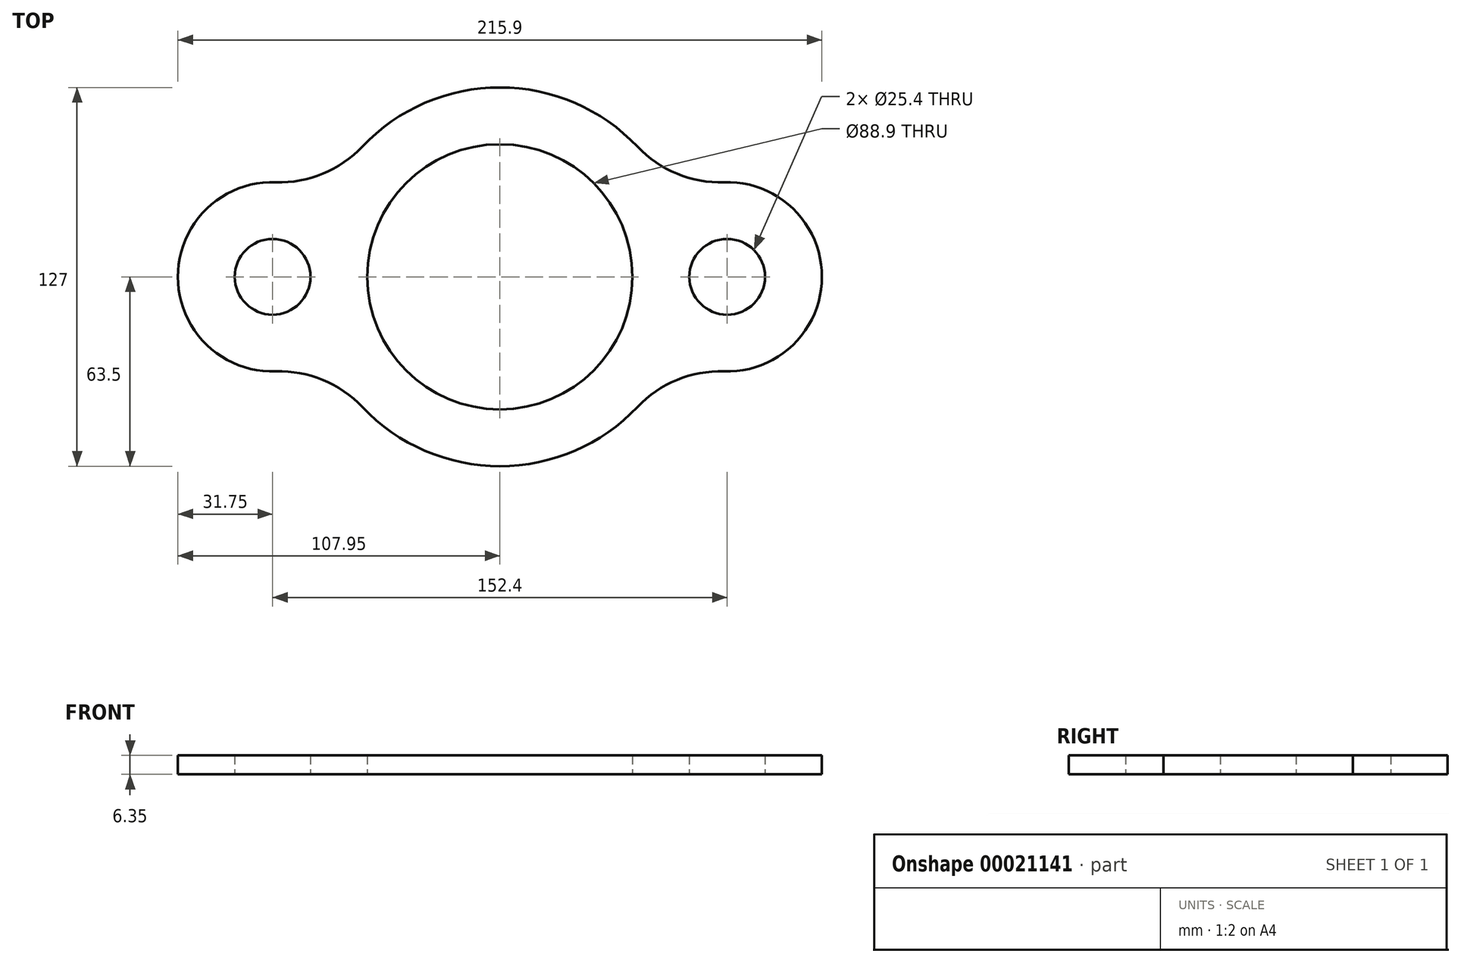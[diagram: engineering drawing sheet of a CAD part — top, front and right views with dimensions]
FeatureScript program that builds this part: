
annotation { "Feature Type Name" : "Feature", "Feature Type Description" : "" }
export const myFeature = defineFeature(function(context is Context, id is Id, definition is map)
    precondition{}
    {
        {
            var Q0;
            Q0=qCreatedBy(makeId("Top.planeOp"),FACE);
            var sketch = newSketch(context, id + "F0", { "sketchPlane" : qUnion([Q0])});
            skArc(sketch, "E0", {"start": v(-46.14, -43.63) * mm, "mid": v(0, -63.5) * mm, "end": v(46.14, -43.63) * mm});
            skCircle(sketch, "E1", {"center": v(0, 0) * mm, "radius": 44.45 * mm});
            skLineSegment(sketch, "E2", {"start": v(0, 0) * mm, "end": v(-113.89, 0) * mm});
            skLineSegment(sketch, "E3", {"start": v(-113.89, 0) * mm, "end": v(113.62, 0) * mm});
            skCircle(sketch, "E4", {"center": v(-76.2, 0) * mm, "radius": 12.7 * mm});
            skCircle(sketch, "E5", {"center": v(76.2, 0) * mm, "radius": 12.7 * mm});
            skArc(sketch, "E6", {"start": v(-75.12, 31.73) * mm, "mid": v(-107.95, 0) * mm, "end": v(-75.12, -31.73) * mm});
            skArc(sketch, "E7", {"start": v(75.12, -31.73) * mm, "mid": v(107.95, 0) * mm, "end": v(75.12, 31.73) * mm});
            skArc(sketch, "E8.trimOffspring", {"start": v(46.14, 43.63) * mm, "mid": v(0, 63.5) * mm, "end": v(-46.14, 43.63) * mm});
            skPoint(sketch, "E9.visualSharp", {"position": v(-57.94, -25.98) * mm});
            skArc(sketch, "E9.filletArc", {"start": v(-46.14, -43.63) * mm, "mid": v(-59.35, -34.56) * mm, "end": v(-75.12, -31.73) * mm});
            skPoint(sketch, "E10.visualSharp", {"position": v(-57.94, 25.98) * mm});
            skArc(sketch, "E10.filletArc", {"start": v(-75.12, 31.73) * mm, "mid": v(-59.35, 34.56) * mm, "end": v(-46.14, 43.63) * mm});
            skPoint(sketch, "E11.visualSharp", {"position": v(57.94, 25.98) * mm});
            skArc(sketch, "E11.filletArc", {"start": v(46.14, 43.63) * mm, "mid": v(59.35, 34.56) * mm, "end": v(75.12, 31.73) * mm});
            skPoint(sketch, "E12.visualSharp", {"position": v(57.94, -25.98) * mm});
            skArc(sketch, "E12.filletArc", {"start": v(75.12, -31.73) * mm, "mid": v(59.35, -34.56) * mm, "end": v(46.14, -43.63) * mm});
            skSolve(sketch);
        }
        {
            var Q0;
            Q0=makeQuery(id+"F0.imprint","IMPRINT",FACE,{"disambiguationData":[TD([[makeQuery(id+"F0.imprint","IMPRINT",EDGE,{"derivedFrom":sQuery(id+"F0.wireOp",EDGE,"E8.trimOffspring")}),1.0]])]});
            var Q1;
            Q1=makeQuery(id+"F0.imprint","IMPRINT",FACE,{"disambiguationData":[TD([[makeQuery(id+"F0.imprint","IMPRINT",EDGE,{"derivedFrom":sQuery(id+"F0.wireOp",EDGE,"E0")}),1.0]])]});
            extrude(context, id + "F1", {"entities" : qUnion([Q0, Q1]), "depth" : 6.35 * mm});
        }
    });
